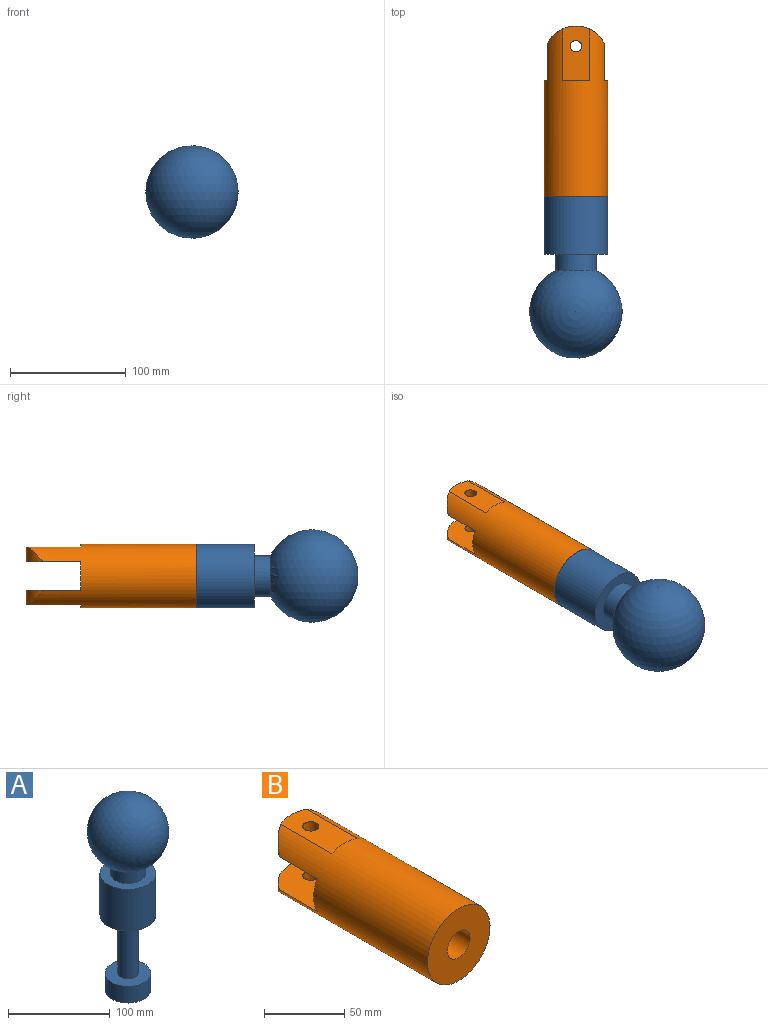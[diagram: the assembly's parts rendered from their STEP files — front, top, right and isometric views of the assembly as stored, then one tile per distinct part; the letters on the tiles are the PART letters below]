
ASSEMBLY  parts=2 mates=1
PART A: 9 faces, bbox 80x80x230 mm
  f0: cylinder r=17.5mm len=35mm, axis (0,0,-1), area 1542.8mm2, adj f6,f8
  f1: cylinder r=22.5mm len=45mm, axis (0,0,-1), area 2827.4mm2, adj f2,f3
  f2: plane 45x45mm, normal (0,0,1), area 1276.3mm2, adj f1,f4
  f3: plane 45x45mm, normal (0,0,-1), area 1590.4mm2, adj f1
  f4: cylinder r=10mm len=70mm, axis (0,0,-1), area 4398.2mm2, adj f2,f7
  f5: cylinder r=27.5mm len=55mm, axis (0,0,-1), area 8639.4mm2, adj f6,f7
  f6: plane 55x55mm, normal (0,0,1), area 1413.7mm2, adj f0,f5
  f7: plane 55x55mm, normal (0,0,-1), area 2061.7mm2, adj f4,f5
  f8: sphere r=40mm, area 19093mm2, adj f0
PART B: 17 faces, bbox 55x147.5x55 mm
  f0: cylinder r=27.5mm len=48.99mm, axis (0,0,-1), area 552.4mm2, adj f1,f4,f15
  f1: cylinder r=27.5mm len=145mm, axis (0,1,0), area 20185.3mm2, adj f0,f3,f4,f5,f6,f7,f10,f14
  f2: cylinder r=5mm len=12.5mm, axis (0,0,-1), area 392.7mm2, adj f4,f15
  f3: cylinder r=27.5mm len=48.99mm, axis (0,0,-1), area 552.4mm2, adj f1,f5,f16
  f4: plane 47.5x22.91mm, normal (0,0,1), area 991.1mm2, adj f0,f1,f2,f6
  f5: plane 47.5x22.91mm, normal (0,0,-1), area 991.1mm2, adj f1,f3,f7,f13
  f6: plane 22.91x2.5mm, normal (0,1,0), area 38.5mm2, adj f1,f4
  f7: plane 22.91x2.5mm, normal (0,1,0), area 38.5mm2, adj f1,f5
  f8: plane 45x45mm, normal (0,1,0), area 1276.3mm2, adj f9,f12
  f9: cylinder r=10mm len=20mm, axis (0,1,0), area 1256.6mm2, adj f8,f10
  f10: plane 55x55mm, normal (0,-1,0), area 2061.7mm2, adj f1,f9
  f11: plane 45x45mm, normal (0,-1,0), area 1590.4mm2, adj f12
  f12: cylinder r=22.5mm len=70mm, axis (0,-1,0), area 9896mm2, adj f8,f11
  f13: cylinder r=5mm len=12.5mm, axis (0,0,-1), area 392.7mm2, adj f5,f16
  f14: plane 55x25mm, normal (0,1,0), area 1326.1mm2, adj f1,f15,f16
  f15: plane 48.99x47.5mm, normal (0,0,-1), area 2038.5mm2, adj f0,f1,f2,f14
  f16: plane 48.99x47.5mm, normal (0,0,1), area 2038.5mm2, adj f1,f3,f13,f14
PLACE A rot(axis=(1,0,0),90deg) t=(0,-10,0)mm
PLACE B at identity fixed
MATE cylindrical A.f1 <-> B.f12  axis (0,1,0) through (0,-10,0)mm
